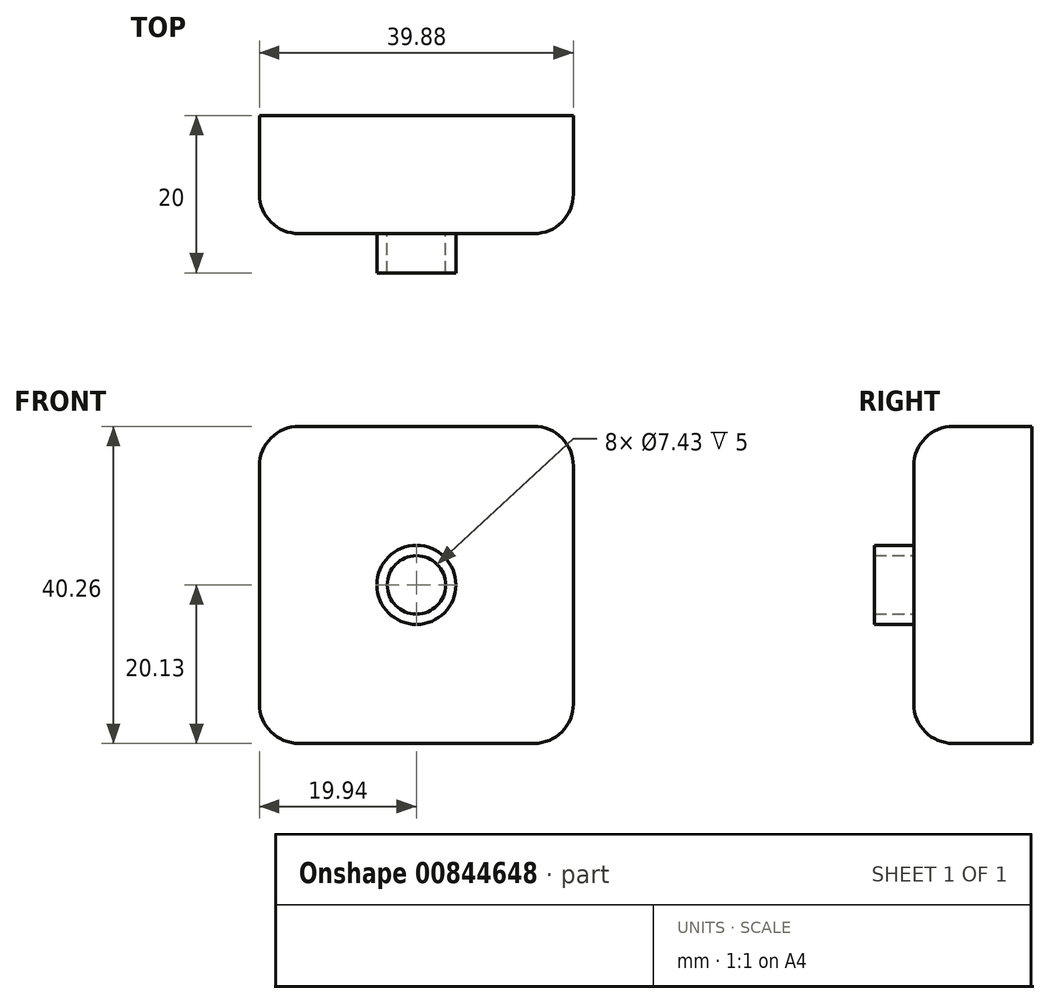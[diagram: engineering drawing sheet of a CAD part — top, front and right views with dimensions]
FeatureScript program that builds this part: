
annotation { "Feature Type Name" : "Feature", "Feature Type Description" : "" }
export const myFeature = defineFeature(function(context is Context, id is Id, definition is map)
    precondition{}
    {
        {
            var Q0;
            Q0=qCreatedBy(makeId("Front.planeOp"),FACE);
            var sketch = newSketch(context, id + "F0", { "sketchPlane" : qUnion([Q0])});
            skLineSegment(sketch, "E0.bottom", {"start": v(19.94, -20.13) * mm, "end": v(-19.94, -20.13) * mm});
            skLineSegment(sketch, "E0.top", {"start": v(19.94, 20.13) * mm, "end": v(-19.94, 20.13) * mm});
            skLineSegment(sketch, "E0.left", {"start": v(19.94, -20.13) * mm, "end": v(19.94, 20.13) * mm});
            skLineSegment(sketch, "E0.right", {"start": v(-19.94, -20.13) * mm, "end": v(-19.94, 20.13) * mm});
            skPoint(sketch, "E0.middle", {"position": v(0, 0) * mm});
            skSolve(sketch);
        }
        {
            var Q0;
            Q0=makeQuery(id+"F0.imprint","IMPRINT",FACE,{"disambiguationData":[TD([[makeQuery(id+"F0.imprint","IMPRINT",EDGE,{"derivedFrom":sQuery(id+"F0.wireOp",EDGE,"E0.bottom")}),-1.0]])]});
            extrude(context, id + "F1", {"entities" : qUnion([Q0]), "depth" : 15 * mm, "offsetDistance" : 25 * mm});
        }
        {
            var Q0;
            Q0=makeQuery(id+"F1.opExtrude","CAP_FACE",FACE,{"disambiguationData":[OSD([sQuery(id+"F0.wireOp",EDGE,"E0.bottom"),sQuery(id+"F0.wireOp",EDGE,"E0.top"),sQuery(id+"F0.wireOp",EDGE,"E0.left"),sQuery(id+"F0.wireOp",EDGE,"E0.right")])],"isStart":false});
            var Q1;
            Q1=makeQuery(id+"F1.opExtrude","SWEPT_EDGE",EDGE,{"disambiguationData":[OSD([sQuery(id+"F0.wireOp",EDGE,"E0.bottom"),sQuery(id+"F0.wireOp",EDGE,"E0.right")])]});
            var Q2;
            Q2=makeQuery(id+"F1.opExtrude","SWEPT_EDGE",EDGE,{"disambiguationData":[OSD([sQuery(id+"F0.wireOp",EDGE,"E0.top"),sQuery(id+"F0.wireOp",EDGE,"E0.right")])]});
            var Q3;
            Q3=makeQuery(id+"F1.opExtrude","SWEPT_EDGE",EDGE,{"disambiguationData":[OSD([sQuery(id+"F0.wireOp",EDGE,"E0.bottom"),sQuery(id+"F0.wireOp",EDGE,"E0.left")])]});
            var Q4;
            Q4=makeQuery(id+"F1.opExtrude","SWEPT_EDGE",EDGE,{"disambiguationData":[OSD([sQuery(id+"F0.wireOp",EDGE,"E0.top"),sQuery(id+"F0.wireOp",EDGE,"E0.left")])]});
            fillet(context, id + "F2", {"entities" : qUnion([Q0, Q1, Q2, Q3, Q4]), "radius" : 5 * mm, "tangentPropagation" : true, "allowEdgeOverflow" : false});
        }
        {
            var Q0;
            Q0=makeQuery(id+"F1.opExtrude","CAP_FACE",FACE,{"disambiguationData":[OSD([sQuery(id+"F0.wireOp",EDGE,"E0.bottom"),sQuery(id+"F0.wireOp",EDGE,"E0.top"),sQuery(id+"F0.wireOp",EDGE,"E0.left"),sQuery(id+"F0.wireOp",EDGE,"E0.right")])],"isStart":false});
            var sketch = newSketch(context, id + "F3", { "sketchPlane" : qUnion([Q0])});
            skCircle(sketch, "E1", {"center": v(0, 0) * mm, "radius": 3.71 * mm});
            skCircle(sketch, "E2", {"center": v(0, 0) * mm, "radius": 5.02 * mm});
            skSolve(sketch);
        }
        {
            var Q0;
            Q0=makeQuery(id+"F3.imprint","IMPRINT",FACE,{"disambiguationData":[TD([[makeQuery(id+"F3.imprint","IMPRINT",EDGE,{"derivedFrom":sQuery(id+"F3.wireOp",EDGE,"E1")}),-1.0]])]});
            extrude(context, id + "F4", {"entities" : qUnion([Q0]), "depth" : 5 * mm, "offsetDistance" : 25 * mm});
        }
    });
